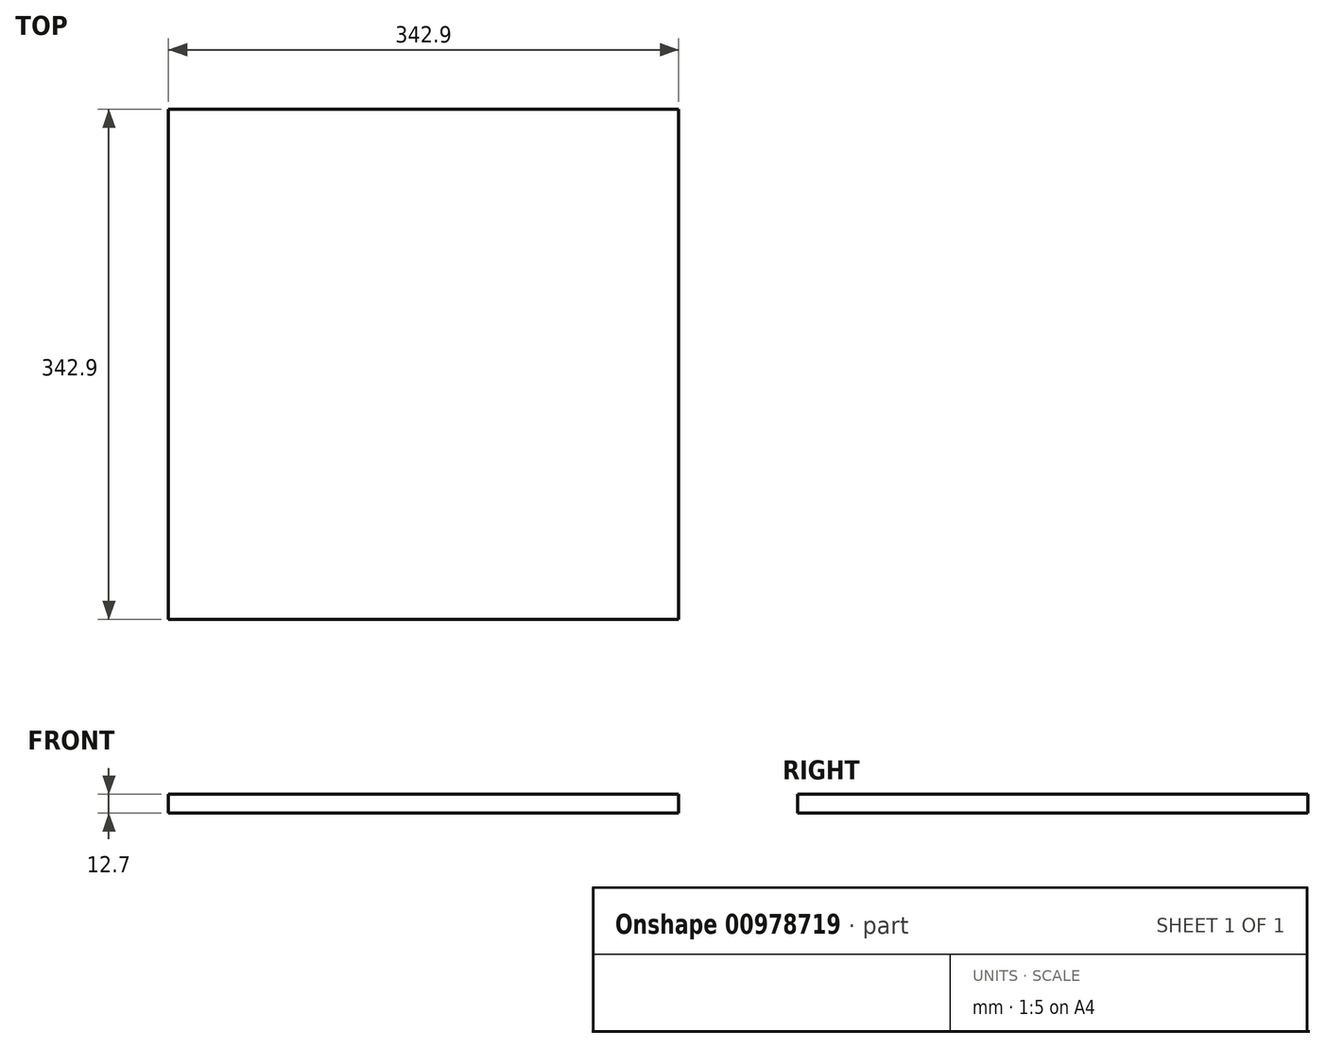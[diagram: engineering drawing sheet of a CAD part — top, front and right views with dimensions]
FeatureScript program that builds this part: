
annotation { "Feature Type Name" : "Feature", "Feature Type Description" : "" }
export const myFeature = defineFeature(function(context is Context, id is Id, definition is map)
    precondition{}
    {
        {
            var Q0;
            Q0=qCreatedBy(makeId("Top.planeOp"),FACE);
            var sketch = newSketch(context, id + "F0", { "sketchPlane" : qUnion([Q0])});
            skLineSegment(sketch, "E0.bottom", {"start": v(-171.45, 171.45) * mm, "end": v(171.45, 171.45) * mm});
            skLineSegment(sketch, "E0.top", {"start": v(-171.45, -171.45) * mm, "end": v(171.45, -171.45) * mm});
            skLineSegment(sketch, "E0.left", {"start": v(-171.45, 171.45) * mm, "end": v(-171.45, -171.45) * mm});
            skLineSegment(sketch, "E0.right", {"start": v(171.45, 171.45) * mm, "end": v(171.45, -171.45) * mm});
            skPoint(sketch, "E0.middle", {"position": v(0, 0) * mm});
            skSolve(sketch);
        }
        {
            var Q0;
            Q0=makeQuery(id+"F0.imprint","IMPRINT",FACE,{"disambiguationData":[TD([[makeQuery(id+"F0.imprint","IMPRINT",EDGE,{"derivedFrom":sQuery(id+"F0.wireOp",EDGE,"E0.bottom")}),-1.0]])]});
            extrude(context, id + "F1", {"entities" : qUnion([Q0]), "depth" : 12.7 * mm, "offsetDistance" : 25.4 * mm});
        }
    });
